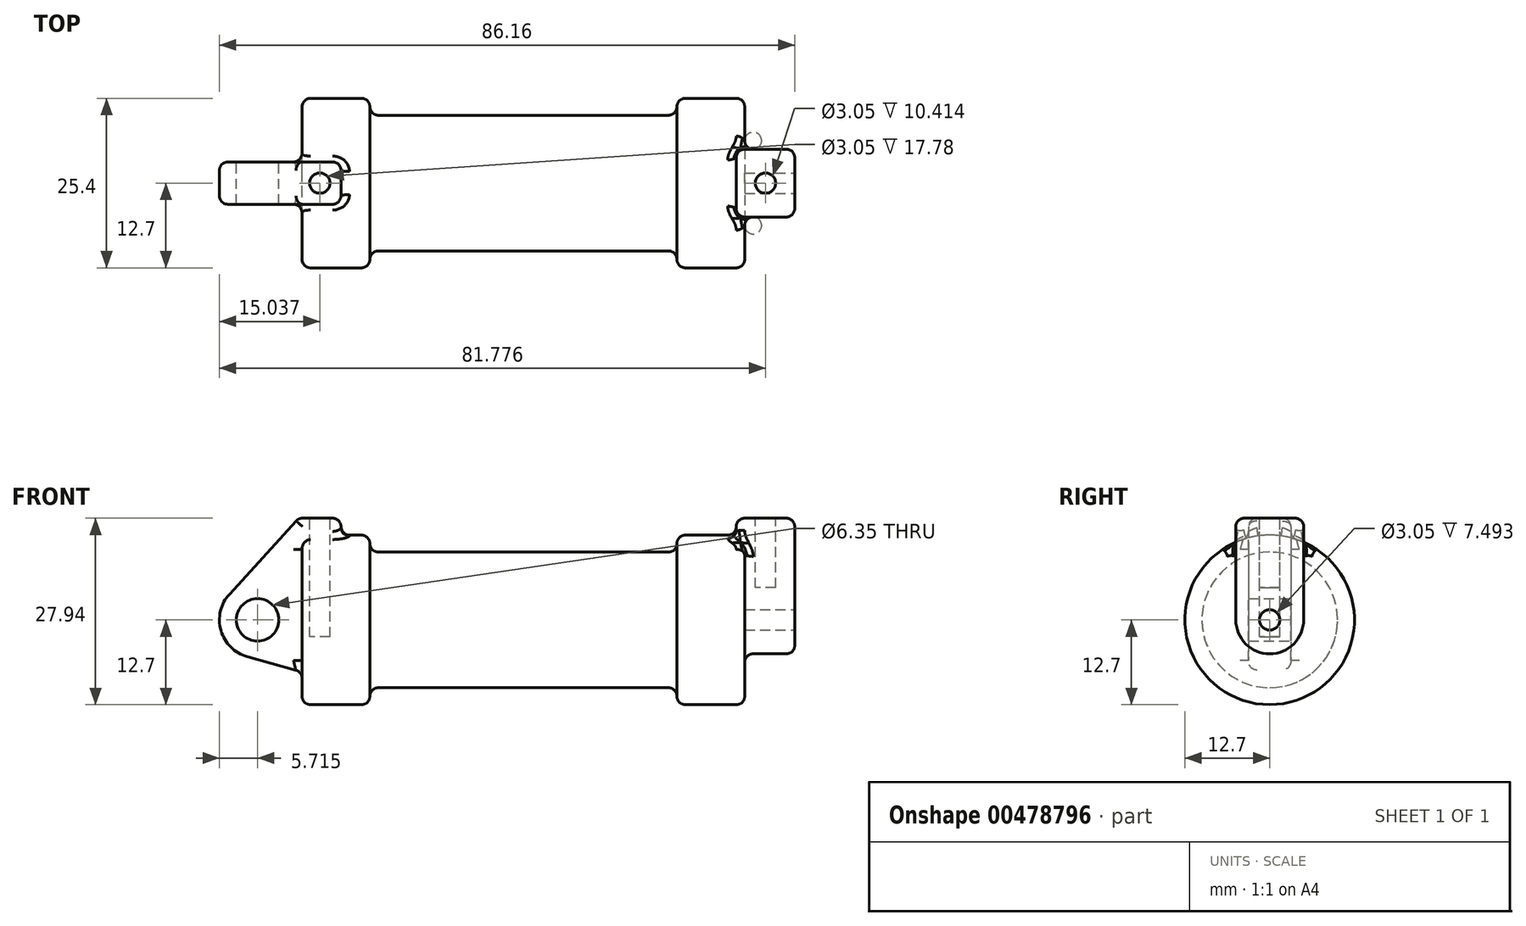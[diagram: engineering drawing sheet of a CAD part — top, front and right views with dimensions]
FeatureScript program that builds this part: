
annotation { "Feature Type Name" : "Feature", "Feature Type Description" : "" }
export const myFeature = defineFeature(function(context is Context, id is Id, definition is map)
    precondition{}
    {
        {
            var Q0;
            Q0=qCreatedBy(makeId("Front.planeOp"),FACE);
            var sketch = newSketch(context, id + "F0", { "sketchPlane" : qUnion([Q0])});
            skLineSegment(sketch, "E0", {"start": v(0, 0) * mm, "end": v(0, 12.7) * mm});
            skLineSegment(sketch, "E1", {"start": v(0, 12.7) * mm, "end": v(10.16, 12.7) * mm});
            skLineSegment(sketch, "E2", {"start": v(10.16, 12.7) * mm, "end": v(10.16, 10.16) * mm});
            skLineSegment(sketch, "E3", {"start": v(10.16, 10.16) * mm, "end": v(56.13, 10.16) * mm});
            skLineSegment(sketch, "E4", {"start": v(56.13, 10.16) * mm, "end": v(56.13, 12.7) * mm});
            skLineSegment(sketch, "E5", {"start": v(56.13, 12.7) * mm, "end": v(66.3, 12.7) * mm});
            skLineSegment(sketch, "E6", {"start": v(66.3, 12.7) * mm, "end": v(66.3, 0) * mm});
            skLineSegment(sketch, "E7", {"start": v(66.3, 0) * mm, "end": v(0, 0) * mm});
            skLineSegment(sketch, "E8", {"start": v(5.84, 15.24) * mm, "end": v(-0.5, 15.24) * mm});
            skLineSegment(sketch, "E9", {"start": v(-0.5, 15.24) * mm, "end": v(-10.88, 3.85) * mm});
            skLineSegment(sketch, "E10", {"start": v(0, 0) * mm, "end": v(-6.65, 0) * mm});
            skCircle(sketch, "E11", {"center": v(-6.65, 0) * mm, "radius": 5.72 * mm});
            skCircle(sketch, "E12", {"center": v(-6.65, 0) * mm, "radius": 3.18 * mm});
            skLineSegment(sketch, "E13", {"start": v(5.84, 15.24) * mm, "end": v(5.84, -9.4) * mm});
            skLineSegment(sketch, "E14", {"start": v(5.84, -9.4) * mm, "end": v(-8.18, -5.5) * mm});
            skSolve(sketch);
        }
        {
            var Q0;
            {var subQ0=sQuery(id+"F0.wireOp",EDGE,"E2");Q0=makeQuery(id+"F0.imprint","IMPRINT",FACE,{"disambiguationData":[TD([[makeQuery(id+"F0.imprint","IMPRINT",EDGE,{"derivedFrom":subQ0}),-1.0]])]});}
            var Q1;
            {var subQ0=sQuery(id+"F0.wireOp",EDGE,"E0");Q1=makeQuery(id+"F0.imprint","IMPRINT",FACE,{"disambiguationData":[TD([[makeQuery(id+"F0.imprint","IMPRINT",EDGE,{"derivedFrom":subQ0}),-1.0]])]});}
            var Q2;
            Q2=sQuery(id+"F0.wireOp",EDGE,"E7");
            revolve(context, id + "F1", {"entities" : qUnion([Q0, Q1]), "axis" : qUnion([Q2]), "revolveType" : RevolveType.FULL});
        }
        {
            var Q0;
            Q0=makeQuery(id+"F1.opRevolve","SWEPT_FACE",FACE,{"disambiguationData":[OSD([sQuery(id+"F0.wireOp",EDGE,"E6")])]});
            var sketch = newSketch(context, id + "F2", { "sketchPlane" : qUnion([Q0])});
            skCircle(sketch, "E15", {"center": v(0, 0) * mm, "radius": 1.52 * mm});
            skCircle(sketch, "E16", {"center": v(0, 0) * mm, "radius": 5.08 * mm});
            skLineSegment(sketch, "E17", {"start": v(-5.08, 0) * mm, "end": v(-5.08, 15.24) * mm});
            skLineSegment(sketch, "E18", {"start": v(5.08, 0) * mm, "end": v(5.08, 15.24) * mm});
            skLineSegment(sketch, "E19", {"start": v(-5.08, 15.24) * mm, "end": v(5.08, 15.24) * mm});
            skSolve(sketch);
        }
        {
            var Q0;
            {var subQ0=sQuery(id+"F2.wireOp",EDGE,"E17");var subQ1=sQuery(id+"F2.wireOp",EDGE,"E16");var subQ2=makeQuery(id+"F2.imprint","INTERSECT",VERTEX,{"derivedFrom":[subQ1,subQ0]});Q0=makeQuery(id+"F2.imprint","IMPRINT",FACE,{"disambiguationData":[TD([[makeQuery(id+"F2.imprint","IMPRINT",EDGE,{"disambiguationData":[TD([[subQ2,1.0]])],"derivedFrom":subQ1}),-1.0]])]});}
            var Q1;
            Q1=makeQuery(id+"F2.imprint","IMPRINT",FACE,{"disambiguationData":[TD([[makeQuery(id+"F2.imprint","IMPRINT",EDGE,{"derivedFrom":sQuery(id+"F2.wireOp",EDGE,"E15")}),-1.0]])]});
            var Q2;
            {var subQ0=sQuery(id+"F2.wireOp",EDGE,"E19");Q2=makeQuery(id+"F2.imprint","IMPRINT",FACE,{"disambiguationData":[TD([[makeQuery(id+"F2.imprint","IMPRINT",EDGE,{"derivedFrom":subQ0}),-1.0]])]});}
            extrude(context, id + "F3", {"entities" : qUnion([Q0, Q1, Q2]), "operationType" : NewBodyOperationType.ADD, "oppositeDirection" : true, "depth" : 1.27 * mm, "hasSecondDirection" : true, "secondDirectionOppositeDirection" : false, "secondDirectionDepth" : 7.5 * mm});
        }
        {
            var Q0;
            {var subQ0=sQuery(id+"F0.wireOp",EDGE,"E0");Q0=makeQuery(id+"F0.imprint","IMPRINT",FACE,{"disambiguationData":[TD([[makeQuery(id+"F0.imprint","IMPRINT",EDGE,{"derivedFrom":subQ0}),-1.0]])]});}
            var Q1;
            {var subQ1=sQuery(id+"F0.wireOp",EDGE,"E0");Q1=makeQuery(id+"F0.imprint","IMPRINT",FACE,{"disambiguationData":[TD([[makeQuery(id+"F0.imprint","IMPRINT",EDGE,{"derivedFrom":subQ1}),1.0]])]});}
            var Q2;
            {var subQ0=sQuery(id+"F0.wireOp",EDGE,"E14");Q2=makeQuery(id+"F0.imprint","IMPRINT",FACE,{"disambiguationData":[TD([[makeQuery(id+"F0.imprint","IMPRINT",EDGE,{"derivedFrom":subQ0}),-1.0]])]});}
            var Q3;
            {var subQ5=sQuery(id+"F0.wireOp",EDGE,"E12");Q3=makeQuery(id+"F0.imprint","IMPRINT",FACE,{"disambiguationData":[TD([[makeQuery(id+"F0.imprint","IMPRINT",EDGE,{"derivedFrom":subQ5}),-1.0]])]});}
            extrude(context, id + "F4", {"entities" : qUnion([Q0, Q1, Q2, Q3]), "endBound" : BoundingType.SYMMETRIC, "depth" : 6.35 * mm});
        }
        {
            var Q0;
            Q0=makeQuery(id+"F4.opExtrude","SWEPT_FACE",FACE,{"disambiguationData":[OSD([sQuery(id+"F0.wireOp",EDGE,"E8")])]});
            var sketch = newSketch(context, id + "F5", { "sketchPlane" : qUnion([Q0])});
            skCircle(sketch, "E20", {"center": v(2.67, 0) * mm, "radius": 1.52 * mm});
            skSolve(sketch);
        }
        {
            var Q0;
            Q0=makeQuery(id+"F5.imprint","IMPRINT",FACE,{"disambiguationData":[TD([[makeQuery(id+"F5.imprint","IMPRINT",EDGE,{"derivedFrom":sQuery(id+"F5.wireOp",EDGE,"E20")}),1.0]])]});
            extrude(context, id + "F6", {"entities" : qUnion([Q0]), "operationType" : NewBodyOperationType.REMOVE, "oppositeDirection" : true, "depth" : 17.78 * mm});
        }
        {
            var Q0;
            Q0=makeQuery(id+"F3.opExtrude","SWEPT_FACE",FACE,{"disambiguationData":[OSD([sQuery(id+"F2.wireOp",EDGE,"E19")])]});
            var sketch = newSketch(context, id + "F7", { "sketchPlane" : qUnion([Q0])});
            skCircle(sketch, "E21", {"center": v(69.4, 0) * mm, "radius": 1.52 * mm});
            skSolve(sketch);
        }
        {
            var Q0;
            Q0=makeQuery(id+"F7.imprint","IMPRINT",FACE,{"disambiguationData":[TD([[makeQuery(id+"F7.imprint","IMPRINT",EDGE,{"derivedFrom":sQuery(id+"F7.wireOp",EDGE,"E21")}),1.0]])]});
            extrude(context, id + "F8", {"entities" : qUnion([Q0]), "operationType" : NewBodyOperationType.REMOVE, "oppositeDirection" : true, "depth" : 10.4 * mm});
        }
        {
            var Q0;
            Q0=makeQuery(id+"F1.opRevolve","SWEPT_EDGE",EDGE,{"disambiguationData":[OSD([sQuery(id+"F0.wireOp",EDGE,"E0"),sQuery(id+"F0.wireOp",EDGE,"E1")])]});
            var Q1;
            Q1=makeQuery(id+"F1.opRevolve","SWEPT_EDGE",EDGE,{"disambiguationData":[OSD([sQuery(id+"F0.wireOp",EDGE,"E1"),sQuery(id+"F0.wireOp",EDGE,"E2")])]});
            var Q2;
            Q2=makeQuery(id+"F4.opExtrude","CAP_EDGE",EDGE,{"disambiguationData":[OSD([sQuery(id+"F0.wireOp",EDGE,"E14")])],"isStart":false});
            var Q3;
            Q3=makeQuery(id+"F4.opExtrude","CAP_EDGE",EDGE,{"disambiguationData":[OSD([sQuery(id+"F0.wireOp",EDGE,"E11")])],"isStart":false});
            var Q4;
            Q4=makeQuery(id+"F4.opExtrude","CAP_EDGE",EDGE,{"disambiguationData":[OSD([sQuery(id+"F0.wireOp",EDGE,"E8")])],"isStart":false});
            var Q5;
            Q5=makeQuery(id+"F4.opExtrude","CAP_EDGE",EDGE,{"disambiguationData":[OSD([sQuery(id+"F0.wireOp",EDGE,"E13")])],"isStart":false});
            var Q6;
            Q6=makeQuery(id+"F4.opExtrude","CAP_EDGE",EDGE,{"disambiguationData":[OSD([sQuery(id+"F0.wireOp",EDGE,"E9")])],"isStart":false});
            var Q7;
            Q7=makeQuery(id+"F4.opExtrude","SWEPT_EDGE",EDGE,{"disambiguationData":[OSD([sQuery(id+"F0.wireOp",EDGE,"E8"),sQuery(id+"F0.wireOp",EDGE,"E13")])]});
            var Q8;
            Q8=makeQuery(id+"F4.opExtrude","CAP_EDGE",EDGE,{"disambiguationData":[OSD([sQuery(id+"F0.wireOp",EDGE,"E13")])],"isStart":true});
            var Q9;
            Q9=makeQuery(id+"F4.opExtrude","CAP_EDGE",EDGE,{"disambiguationData":[OSD([sQuery(id+"F0.wireOp",EDGE,"E8")])],"isStart":true});
            var Q10;
            Q10=makeQuery(id+"F1.opRevolve","SWEPT_EDGE",EDGE,{"disambiguationData":[OSD([sQuery(id+"F0.wireOp",EDGE,"E2"),sQuery(id+"F0.wireOp",EDGE,"E3")])]});
            var Q11;
            Q11=makeQuery(id+"F4.opExtrude","CAP_EDGE",EDGE,{"disambiguationData":[OSD([sQuery(id+"F0.wireOp",EDGE,"E9")])],"isStart":true});
            var Q12;
            Q12=makeQuery(id+"F4.opExtrude","CAP_EDGE",EDGE,{"disambiguationData":[OSD([sQuery(id+"F0.wireOp",EDGE,"E11")])],"isStart":true});
            var Q13;
            Q13=makeQuery(id+"F4.opExtrude","CAP_EDGE",EDGE,{"disambiguationData":[OSD([sQuery(id+"F0.wireOp",EDGE,"E14")])],"isStart":true});
            fillet(context, id + "F9", {"entities" : qUnion([Q0, Q1, Q2, Q3, Q4, Q5, Q6, Q7, Q8, Q9, Q10, Q11, Q12, Q13]), "radius" : 1.27 * mm, "tangentPropagation" : true, "allowEdgeOverflow" : false});
        }
        {
            var Q0;
            Q0=makeQuery(id+"F1.opRevolve","SWEPT_BODY",BODY,{"disambiguationData":[OSD([sQuery(id+"F0.wireOp",EDGE,"E0"),sQuery(id+"F0.wireOp",EDGE,"E1"),sQuery(id+"F0.wireOp",EDGE,"E2"),sQuery(id+"F0.wireOp",EDGE,"E3"),sQuery(id+"F0.wireOp",EDGE,"E4"),sQuery(id+"F0.wireOp",EDGE,"E5"),sQuery(id+"F0.wireOp",EDGE,"E6"),sQuery(id+"F0.wireOp",EDGE,"E7")])]});
            var Q1;
            Q1=makeQuery(id+"F4.opExtrude","SWEPT_BODY",BODY,{"disambiguationData":[OSD([sQuery(id+"F0.wireOp",EDGE,"E8"),sQuery(id+"F0.wireOp",EDGE,"E9"),sQuery(id+"F0.wireOp",EDGE,"E11"),sQuery(id+"F0.wireOp",EDGE,"E12"),sQuery(id+"F0.wireOp",EDGE,"E13"),sQuery(id+"F0.wireOp",EDGE,"E14")])]});
            booleanBodies(context, id + "F10", {"operationType" : BooleanOperationType.UNION, "tools" : qUnion([Q0, Q1])});
        }
        {
            var Q0;
            Q0=makeQuery(id+"F10.opBoolean","INTERSECT",EDGE,{"derivedFrom":[makeQuery(id+"F1.opRevolve","SWEPT_FACE",FACE,{"disambiguationData":[OSD([sQuery(id+"F0.wireOp",EDGE,"E1")])]}),makeQuery(id+"F4.opExtrude","CAP_FACE",FACE,{"disambiguationData":[OSD([sQuery(id+"F0.wireOp",EDGE,"E8"),sQuery(id+"F0.wireOp",EDGE,"E9"),sQuery(id+"F0.wireOp",EDGE,"E11"),sQuery(id+"F0.wireOp",EDGE,"E12"),sQuery(id+"F0.wireOp",EDGE,"E13"),sQuery(id+"F0.wireOp",EDGE,"E14")])],"isStart":false})]});
            var Q1;
            {var subQ0=sQuery(id+"F0.wireOp",EDGE,"E13");Q1=makeQuery(id+"F10.opBoolean","INTERSECT",EDGE,{"derivedFrom":[makeQuery(id+"F9.opFillet","BLEND_FACE",FACE,{"disambiguationData":[OSD([subQ0]),TDD([makeQuery(id+"F4.opExtrude","CAP_EDGE",EDGE,{"disambiguationData":[OSD([subQ0])],"isStart":false})])]}),makeQuery(id+"F1.opRevolve","SWEPT_FACE",FACE,{"disambiguationData":[OSD([sQuery(id+"F0.wireOp",EDGE,"E1")])]})]});}
            var Q2;
            Q2=makeQuery(id+"F10.opBoolean","INTERSECT",EDGE,{"derivedFrom":[makeQuery(id+"F1.opRevolve","SWEPT_FACE",FACE,{"disambiguationData":[OSD([sQuery(id+"F0.wireOp",EDGE,"E1")])]}),makeQuery(id+"F4.opExtrude","SWEPT_FACE",FACE,{"disambiguationData":[OSD([sQuery(id+"F0.wireOp",EDGE,"E13")])]})]});
            var Q3;
            Q3=makeQuery(id+"F10.opBoolean","INTERSECT",EDGE,{"derivedFrom":[makeQuery(id+"F1.opRevolve","SWEPT_FACE",FACE,{"disambiguationData":[OSD([sQuery(id+"F0.wireOp",EDGE,"E1")])]}),makeQuery(id+"F4.opExtrude","CAP_FACE",FACE,{"disambiguationData":[OSD([sQuery(id+"F0.wireOp",EDGE,"E8"),sQuery(id+"F0.wireOp",EDGE,"E9"),sQuery(id+"F0.wireOp",EDGE,"E11"),sQuery(id+"F0.wireOp",EDGE,"E12"),sQuery(id+"F0.wireOp",EDGE,"E13"),sQuery(id+"F0.wireOp",EDGE,"E14")])],"isStart":true})]});
            var Q4;
            {var subQ0=sQuery(id+"F0.wireOp",EDGE,"E13");Q4=makeQuery(id+"F10.opBoolean","INTERSECT",EDGE,{"derivedFrom":[makeQuery(id+"F9.opFillet","BLEND_FACE",FACE,{"disambiguationData":[OSD([subQ0]),TDD([makeQuery(id+"F4.opExtrude","CAP_EDGE",EDGE,{"disambiguationData":[OSD([subQ0])],"isStart":true})])]}),makeQuery(id+"F1.opRevolve","SWEPT_FACE",FACE,{"disambiguationData":[OSD([sQuery(id+"F0.wireOp",EDGE,"E1")])]})]});}
            var Q5;
            Q5=makeQuery(id+"F10.opBoolean","INTERSECT",EDGE,{"derivedFrom":[makeQuery(id+"F1.opRevolve","SWEPT_FACE",FACE,{"disambiguationData":[OSD([sQuery(id+"F0.wireOp",EDGE,"E0")])]}),makeQuery(id+"F4.opExtrude","CAP_FACE",FACE,{"disambiguationData":[OSD([sQuery(id+"F0.wireOp",EDGE,"E8"),sQuery(id+"F0.wireOp",EDGE,"E9"),sQuery(id+"F0.wireOp",EDGE,"E11"),sQuery(id+"F0.wireOp",EDGE,"E12"),sQuery(id+"F0.wireOp",EDGE,"E13"),sQuery(id+"F0.wireOp",EDGE,"E14")])],"isStart":true})]});
            var Q6;
            Q6=makeQuery(id+"F10.opBoolean","INTERSECT",EDGE,{"derivedFrom":[makeQuery(id+"F9.opFillet","BLEND_FACE",FACE,{"disambiguationData":[OSD([sQuery(id+"F0.wireOp",EDGE,"E0"),sQuery(id+"F0.wireOp",EDGE,"E1")])]}),makeQuery(id+"F4.opExtrude","CAP_FACE",FACE,{"disambiguationData":[OSD([sQuery(id+"F0.wireOp",EDGE,"E8"),sQuery(id+"F0.wireOp",EDGE,"E9"),sQuery(id+"F0.wireOp",EDGE,"E11"),sQuery(id+"F0.wireOp",EDGE,"E12"),sQuery(id+"F0.wireOp",EDGE,"E13"),sQuery(id+"F0.wireOp",EDGE,"E14")])],"isStart":true})]});
            var Q7;
            {var subQ0=sQuery(id+"F0.wireOp",EDGE,"E14");Q7=makeQuery(id+"F10.opBoolean","INTERSECT",EDGE,{"derivedFrom":[makeQuery(id+"F9.opFillet","BLEND_FACE",FACE,{"disambiguationData":[OSD([subQ0]),TDD([makeQuery(id+"F4.opExtrude","CAP_EDGE",EDGE,{"disambiguationData":[OSD([subQ0])],"isStart":true})])]}),makeQuery(id+"F1.opRevolve","SWEPT_FACE",FACE,{"disambiguationData":[OSD([sQuery(id+"F0.wireOp",EDGE,"E0")])]})]});}
            var Q8;
            Q8=makeQuery(id+"F10.opBoolean","INTERSECT",EDGE,{"derivedFrom":[makeQuery(id+"F1.opRevolve","SWEPT_FACE",FACE,{"disambiguationData":[OSD([sQuery(id+"F0.wireOp",EDGE,"E0")])]}),makeQuery(id+"F4.opExtrude","SWEPT_FACE",FACE,{"disambiguationData":[OSD([sQuery(id+"F0.wireOp",EDGE,"E14")])]})]});
            var Q9;
            {var subQ0=sQuery(id+"F0.wireOp",EDGE,"E14");Q9=makeQuery(id+"F10.opBoolean","INTERSECT",EDGE,{"derivedFrom":[makeQuery(id+"F9.opFillet","BLEND_FACE",FACE,{"disambiguationData":[OSD([subQ0]),TDD([makeQuery(id+"F4.opExtrude","CAP_EDGE",EDGE,{"disambiguationData":[OSD([subQ0])],"isStart":false})])]}),makeQuery(id+"F1.opRevolve","SWEPT_FACE",FACE,{"disambiguationData":[OSD([sQuery(id+"F0.wireOp",EDGE,"E0")])]})]});}
            var Q10;
            Q10=makeQuery(id+"F10.opBoolean","INTERSECT",EDGE,{"derivedFrom":[makeQuery(id+"F1.opRevolve","SWEPT_FACE",FACE,{"disambiguationData":[OSD([sQuery(id+"F0.wireOp",EDGE,"E0")])]}),makeQuery(id+"F4.opExtrude","CAP_FACE",FACE,{"disambiguationData":[OSD([sQuery(id+"F0.wireOp",EDGE,"E8"),sQuery(id+"F0.wireOp",EDGE,"E9"),sQuery(id+"F0.wireOp",EDGE,"E11"),sQuery(id+"F0.wireOp",EDGE,"E12"),sQuery(id+"F0.wireOp",EDGE,"E13"),sQuery(id+"F0.wireOp",EDGE,"E14")])],"isStart":false})]});
            var Q11;
            Q11=makeQuery(id+"F10.opBoolean","INTERSECT",EDGE,{"derivedFrom":[makeQuery(id+"F9.opFillet","BLEND_FACE",FACE,{"disambiguationData":[OSD([sQuery(id+"F0.wireOp",EDGE,"E0"),sQuery(id+"F0.wireOp",EDGE,"E1")])]}),makeQuery(id+"F4.opExtrude","CAP_FACE",FACE,{"disambiguationData":[OSD([sQuery(id+"F0.wireOp",EDGE,"E8"),sQuery(id+"F0.wireOp",EDGE,"E9"),sQuery(id+"F0.wireOp",EDGE,"E11"),sQuery(id+"F0.wireOp",EDGE,"E12"),sQuery(id+"F0.wireOp",EDGE,"E13"),sQuery(id+"F0.wireOp",EDGE,"E14")])],"isStart":false})]});
            fillet(context, id + "F11", {"entities" : qUnion([Q0, Q1, Q2, Q3, Q4, Q5, Q6, Q7, Q8, Q9, Q10, Q11]), "radius" : 1.27 * mm, "tangentPropagation" : true, "allowEdgeOverflow" : false});
        }
        {
            var Q0;
            Q0=makeQuery(id+"F1.opRevolve","SWEPT_EDGE",EDGE,{"disambiguationData":[OSD([sQuery(id+"F0.wireOp",EDGE,"E3"),sQuery(id+"F0.wireOp",EDGE,"E4")])]});
            var Q1;
            Q1=makeQuery(id+"F1.opRevolve","SWEPT_EDGE",EDGE,{"disambiguationData":[OSD([sQuery(id+"F0.wireOp",EDGE,"E4"),sQuery(id+"F0.wireOp",EDGE,"E5")])]});
            var Q2;
            Q2=makeQuery(id+"F3.boolean.opBoolean","INTERSECT",EDGE,{"derivedFrom":[makeQuery(id+"F1.opRevolve","SWEPT_FACE",FACE,{"disambiguationData":[OSD([sQuery(id+"F0.wireOp",EDGE,"E5")])]}),makeQuery(id+"F3.opExtrude","CAP_FACE",FACE,{"disambiguationData":[OSD([sQuery(id+"F2.wireOp",EDGE,"E15"),sQuery(id+"F2.wireOp",EDGE,"E16"),sQuery(id+"F2.wireOp",EDGE,"E17"),sQuery(id+"F2.wireOp",EDGE,"E18"),sQuery(id+"F2.wireOp",EDGE,"E19")])],"isStart":false})]});
            var Q3;
            Q3=makeQuery(id+"F3.boolean.opBoolean","INTERSECT",EDGE,{"derivedFrom":[makeQuery(id+"F1.opRevolve","SWEPT_FACE",FACE,{"disambiguationData":[OSD([sQuery(id+"F0.wireOp",EDGE,"E5")])]}),makeQuery(id+"F3.opExtrude","SWEPT_FACE",FACE,{"disambiguationData":[OSD([sQuery(id+"F2.wireOp",EDGE,"E17")])]})]});
            var Q4;
            Q4=makeQuery(id+"F3.opExtrude","SWEPT_EDGE",EDGE,{"disambiguationData":[OSD([sQuery(id+"F2.wireOp",EDGE,"E17"),sQuery(id+"F2.wireOp",EDGE,"E19")])]});
            var Q5;
            Q5=makeQuery(id+"F3.opExtrude","CAP_EDGE",EDGE,{"disambiguationData":[OSD([sQuery(id+"F2.wireOp",EDGE,"E19")])],"isStart":false});
            var Q6;
            Q6=makeQuery(id+"F3.opExtrude","SWEPT_EDGE",EDGE,{"disambiguationData":[OSD([sQuery(id+"F2.wireOp",EDGE,"E18"),sQuery(id+"F2.wireOp",EDGE,"E19")])]});
            var Q7;
            Q7=makeQuery(id+"F3.opExtrude","CAP_EDGE",EDGE,{"disambiguationData":[OSD([sQuery(id+"F2.wireOp",EDGE,"E19")])],"isStart":true});
            var Q8;
            Q8=makeQuery(id+"F1.opRevolve","SWEPT_EDGE",EDGE,{"disambiguationData":[OSD([sQuery(id+"F0.wireOp",EDGE,"E5"),sQuery(id+"F0.wireOp",EDGE,"E6")])]});
            var Q9;
            Q9=makeQuery(id+"F3.opExtrude","CAP_EDGE",EDGE,{"disambiguationData":[OSD([sQuery(id+"F2.wireOp",EDGE,"E17")])],"isStart":false});
            var Q10;
            Q10=makeQuery(id+"F3.opExtrude","CAP_EDGE",EDGE,{"disambiguationData":[OSD([sQuery(id+"F2.wireOp",EDGE,"E17")])],"isStart":true});
            var Q11;
            Q11=makeQuery(id+"F3.boolean.opBoolean","INTERSECT",EDGE,{"derivedFrom":[makeQuery(id+"F1.opRevolve","SWEPT_FACE",FACE,{"disambiguationData":[OSD([sQuery(id+"F0.wireOp",EDGE,"E6")])]}),makeQuery(id+"F3.opExtrude","SWEPT_FACE",FACE,{"disambiguationData":[OSD([sQuery(id+"F2.wireOp",EDGE,"E17")])]})]});
            var Q12;
            Q12=makeQuery(id+"F3.opExtrude","CAP_EDGE",EDGE,{"disambiguationData":[OSD([sQuery(id+"F2.wireOp",EDGE,"E18")])],"isStart":true});
            var Q13;
            Q13=makeQuery(id+"F3.boolean.opBoolean","INTERSECT",EDGE,{"derivedFrom":[makeQuery(id+"F1.opRevolve","SWEPT_FACE",FACE,{"disambiguationData":[OSD([sQuery(id+"F0.wireOp",EDGE,"E5")])]}),makeQuery(id+"F3.opExtrude","SWEPT_FACE",FACE,{"disambiguationData":[OSD([sQuery(id+"F2.wireOp",EDGE,"E18")])]})]});
            var Q14;
            Q14=makeQuery(id+"F3.opExtrude","CAP_EDGE",EDGE,{"disambiguationData":[OSD([sQuery(id+"F2.wireOp",EDGE,"E18")])],"isStart":false});
            var Q15;
            Q15=makeQuery(id+"F3.boolean.opBoolean","INTERSECT",EDGE,{"derivedFrom":[makeQuery(id+"F1.opRevolve","SWEPT_FACE",FACE,{"disambiguationData":[OSD([sQuery(id+"F0.wireOp",EDGE,"E6")])]}),makeQuery(id+"F3.opExtrude","SWEPT_FACE",FACE,{"disambiguationData":[OSD([sQuery(id+"F2.wireOp",EDGE,"E18")])]})]});
            var Q16;
            Q16=makeQuery(id+"F3.boolean.opBoolean","INTERSECT",EDGE,{"derivedFrom":[makeQuery(id+"F1.opRevolve","SWEPT_FACE",FACE,{"disambiguationData":[OSD([sQuery(id+"F0.wireOp",EDGE,"E6")])]}),makeQuery(id+"F3.opExtrude","SWEPT_FACE",FACE,{"disambiguationData":[OSD([sQuery(id+"F2.wireOp",EDGE,"E16")])]})]});
            var Q17;
            Q17=makeQuery(id+"F3.opExtrude","CAP_EDGE",EDGE,{"disambiguationData":[OSD([sQuery(id+"F2.wireOp",EDGE,"E16")])],"isStart":true});
            fillet(context, id + "F12", {"entities" : qUnion([Q0, Q1, Q2, Q3, Q4, Q5, Q6, Q7, Q8, Q9, Q10, Q11, Q12, Q13, Q14, Q15, Q16, Q17]), "radius" : 1.27 * mm, "tangentPropagation" : true, "allowEdgeOverflow" : false});
        }
        {
            var Q0;
            Q0=makeQuery(id+"F4.opExtrude","SWEPT_EDGE",EDGE,{"disambiguationData":[OSD([sQuery(id+"F0.wireOp",EDGE,"E8"),sQuery(id+"F0.wireOp",EDGE,"E9")])]});
            fillet(context, id + "F13", {"entities" : qUnion([Q0]), "radius" : 1.27 * mm, "tangentPropagation" : true, "allowEdgeOverflow" : false});
        }
    });
